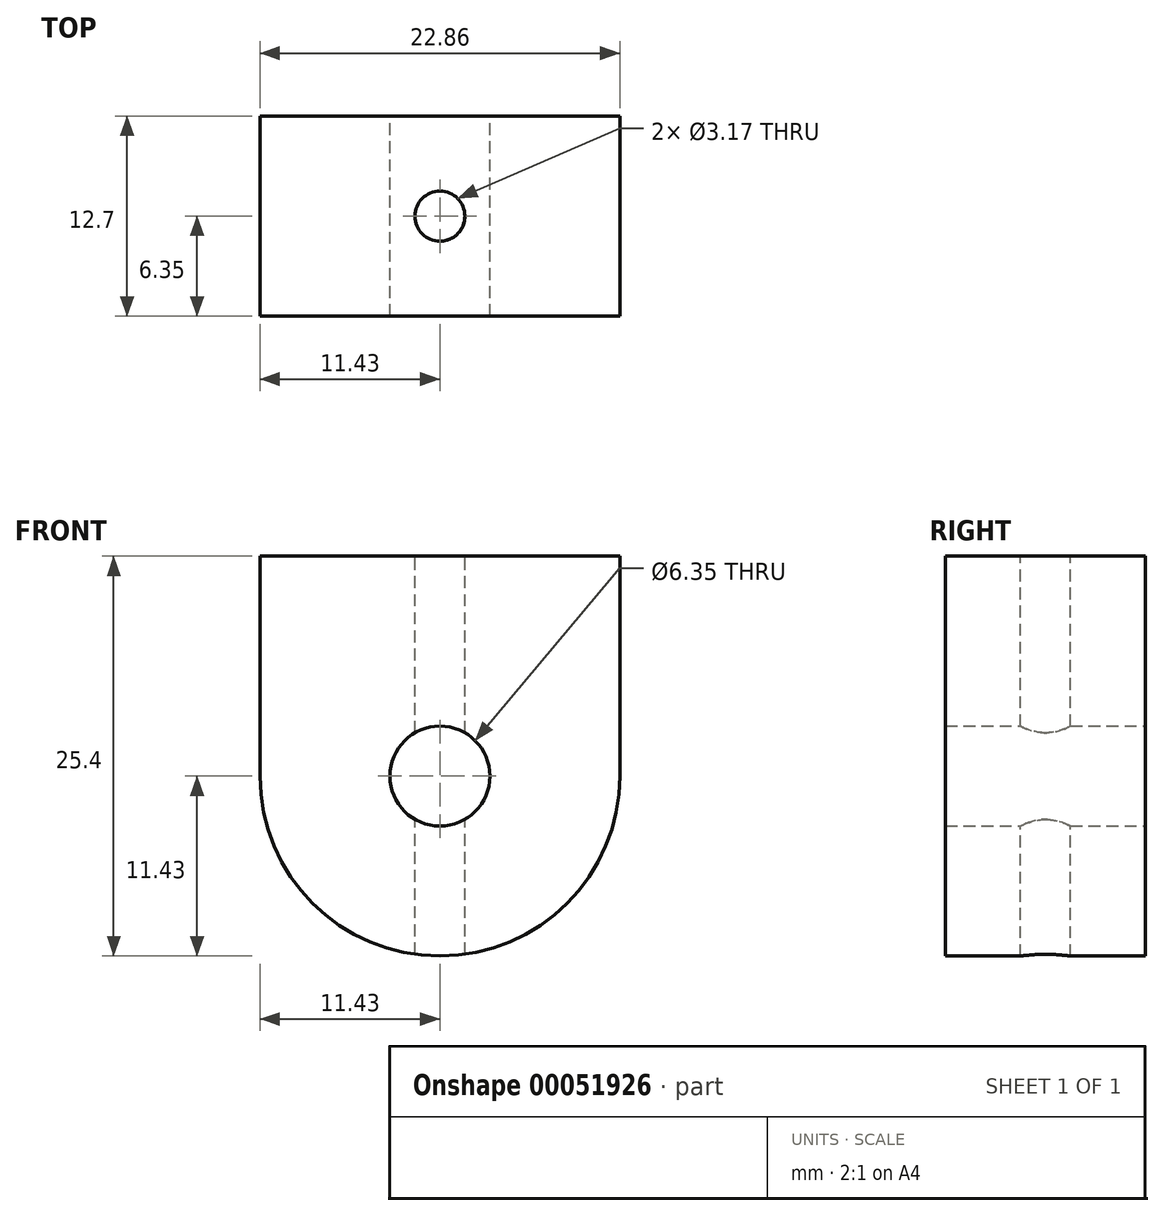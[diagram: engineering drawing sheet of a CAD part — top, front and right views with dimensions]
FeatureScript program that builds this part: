
annotation { "Feature Type Name" : "Feature", "Feature Type Description" : "" }
export const myFeature = defineFeature(function(context is Context, id is Id, definition is map)
    precondition{}
    {
        {
            var Q0;
            Q0=qCreatedBy(makeId("Top.planeOp"),FACE);
            var sketch = newSketch(context, id + "F0", { "sketchPlane" : qUnion([Q0])});
            skLineSegment(sketch, "E0.rect.bottom", {"start": v(12.7, -6.35) * mm, "end": v(-12.7, -6.35) * mm});
            skLineSegment(sketch, "E0.rect.top", {"start": v(12.7, 6.35) * mm, "end": v(-12.7, 6.35) * mm});
            skLineSegment(sketch, "E0.rect.left", {"start": v(12.7, -6.35) * mm, "end": v(12.7, 6.35) * mm});
            skLineSegment(sketch, "E0.rect.right", {"start": v(-12.7, -6.35) * mm, "end": v(-12.7, 6.35) * mm});
            skPoint(sketch, "E0.rect.middle", {"position": v(0, 0) * mm});
            skSolve(sketch);
        }
        {
            var Q0;
            Q0=makeQuery(id+"F0.imprint","IMPRINT",FACE,{"disambiguationData":[TD([[makeQuery(id+"F0.imprint","IMPRINT",EDGE,{"derivedFrom":sQuery(id+"F0.wireOp",EDGE,"E0.rect.bottom")}),-1.0]])]});
            extrude(context, id + "F1", {"entities" : qUnion([Q0]), "depth" : 12.7 * mm});
        }
        {
            var Q0;
            Q0=makeQuery(id+"F1.opExtrude","SWEPT_FACE",FACE,{"disambiguationData":[OSD([sQuery(id+"F0.wireOp",EDGE,"E0.rect.left")])]});
            var sketch = newSketch(context, id + "F2", { "sketchPlane" : qUnion([Q0])});
            skLineSegment(sketch, "E1", {"start": v(-6.35, 12.7) * mm, "end": v(6.35, 0) * mm, "construction": true});
            skLineSegment(sketch, "E2", {"start": v(6.35, 12.7) * mm, "end": v(-6.35, 0) * mm, "construction": true});
            skCircle(sketch, "E3", {"center": v(0, 6.35) * mm, "radius": 1.59 * mm});
            skSolve(sketch);
        }
        {
            var Q0;
            Q0=makeQuery(id+"F2.imprint","IMPRINT",FACE,{"disambiguationData":[TD([[makeQuery(id+"F2.imprint","IMPRINT",EDGE,{"derivedFrom":sQuery(id+"F2.wireOp",EDGE,"E3")}),1.0]])]});
            extrude(context, id + "F3", {"entities" : qUnion([Q0]), "operationType" : NewBodyOperationType.REMOVE, "endBound" : BoundingType.UP_TO_NEXT, "oppositeDirection" : true, "depth" : 25.4 * mm});
        }
        {
            var Q0;
            Q0=qCreatedBy(makeId("Top.planeOp"),FACE);
            var sketch = newSketch(context, id + "F4", { "sketchPlane" : qUnion([Q0])});
            skLineSegment(sketch, "E4.rect.bottom", {"start": v(-38.1, -25.4) * mm, "end": v(38.1, -25.4) * mm});
            skLineSegment(sketch, "E4.rect.top", {"start": v(-38.1, 25.4) * mm, "end": v(38.1, 25.4) * mm});
            skLineSegment(sketch, "E4.rect.left", {"start": v(-38.1, -25.4) * mm, "end": v(-38.1, 25.4) * mm});
            skLineSegment(sketch, "E4.rect.right", {"start": v(38.1, -25.4) * mm, "end": v(38.1, 25.4) * mm});
            skPoint(sketch, "E4.rect.middle", {"position": v(0, 0) * mm});
            skSolve(sketch);
        }
        {
            var Q0;
            Q0=makeQuery(id+"F4.imprint","IMPRINT",FACE,{"disambiguationData":[TD([[makeQuery(id+"F4.imprint","IMPRINT",EDGE,{"derivedFrom":sQuery(id+"F4.wireOp",EDGE,"E4.rect.bottom")}),1.0]])]});
            extrude(context, id + "F5", {"entities" : qUnion([Q0]), "oppositeDirection" : true, "depth" : 1.59 * mm});
        }
        {
            var Q0;
            Q0=qCreatedBy(makeId("Front.planeOp"),FACE);
            var sketch = newSketch(context, id + "F6", { "sketchPlane" : qUnion([Q0])});
            skLineSegment(sketch, "E5.bottom", {"start": v(-12.7, 0) * mm, "end": v(12.7, 0) * mm});
            skLineSegment(sketch, "E5.top", {"start": v(-12.7, 12.7) * mm, "end": v(12.7, 12.7) * mm, "construction": true});
            skLineSegment(sketch, "E5.left", {"start": v(-12.7, 0) * mm, "end": v(-12.7, 12.7) * mm});
            skLineSegment(sketch, "E5.right", {"start": v(12.7, 0) * mm, "end": v(12.7, 12.7) * mm});
            skArc(sketch, "E6", {"start": v(12.7, 12.7) * mm, "mid": v(0, 25.4) * mm, "end": v(-12.7, 12.7) * mm});
            skCircle(sketch, "E7", {"center": v(0, 12.7) * mm, "radius": 3.18 * mm});
            skPoint(sketch, "E8", {"position": v(0, 25.4) * mm});
            skSolve(sketch);
        }
        {
            var Q0;
            Q0=makeQuery(id+"F6.imprint","IMPRINT",FACE,{"disambiguationData":[TD([[makeQuery(id+"F6.imprint","IMPRINT",EDGE,{"derivedFrom":sQuery(id+"F6.wireOp",EDGE,"E5.bottom")}),1.0]])]});
            extrude(context, id + "F7", {"entities" : qUnion([Q0]), "operationType" : NewBodyOperationType.ADD, "depth" : 12.7 * mm, "hasSecondDirection" : true, "secondDirectionOppositeDirection" : true, "secondDirectionDepth" : 12.7 * mm});
        }
        {
            var Q0;
            Q0=qCreatedBy(makeId("Right.planeOp"),FACE);
            var sketch = newSketch(context, id + "F8", { "sketchPlane" : qUnion([Q0])});
            skLineSegment(sketch, "E9.rect.bottom", {"start": v(6.35, 0) * mm, "end": v(-6.35, 0) * mm});
            skLineSegment(sketch, "E9.rect.top", {"start": v(6.35, 65.79) * mm, "end": v(-6.35, 65.79) * mm});
            skLineSegment(sketch, "E9.rect.left", {"start": v(6.35, 0) * mm, "end": v(6.35, 65.79) * mm});
            skLineSegment(sketch, "E9.rect.right", {"start": v(-6.35, 0) * mm, "end": v(-6.35, 65.79) * mm});
            skPoint(sketch, "E9.rect.middle", {"position": v(0, 32.9) * mm});
            skSolve(sketch);
        }
        {
            var Q0;
            Q0=makeQuery(id+"F8.imprint","IMPRINT",FACE,{"disambiguationData":[TD([[makeQuery(id+"F8.imprint","IMPRINT",EDGE,{"derivedFrom":sQuery(id+"F8.wireOp",EDGE,"E9.rect.bottom")}),-1.0]])]});
            extrude(context, id + "F9", {"entities" : qUnion([Q0]), "operationType" : NewBodyOperationType.REMOVE, "endBound" : BoundingType.THROUGH_ALL, "oppositeDirection" : true, "depth" : 25.4 * mm, "hasSecondDirection" : true, "secondDirectionBound" : SecondDirectionBoundingType.THROUGH_ALL, "secondDirectionOppositeDirection" : false, "secondDirectionDepth" : 25.4 * mm});
        }
        {
            var Q0;
            Q0=qCreatedBy(makeId("Front.planeOp"),FACE);
            var sketch = newSketch(context, id + "F10", { "sketchPlane" : qUnion([Q0])});
            skCircle(sketch, "E10.0", {"center": v(0, 12.7) * mm, "radius": 3.18 * mm});
            skLineSegment(sketch, "E11.rect.bottom", {"start": v(11.43, 12.7) * mm, "end": v(-11.43, 12.7) * mm, "construction": true});
            skLineSegment(sketch, "E11.rect.top", {"start": v(11.43, 26.67) * mm, "end": v(-11.43, 26.67) * mm});
            skLineSegment(sketch, "E11.rect.left", {"start": v(11.43, 12.7) * mm, "end": v(11.43, 26.67) * mm});
            skLineSegment(sketch, "E11.rect.right", {"start": v(-11.43, 12.7) * mm, "end": v(-11.43, 26.67) * mm});
            skPoint(sketch, "E11.rect.middle", {"position": v(0, 19.68) * mm});
            skArc(sketch, "E12", {"start": v(-11.43, 12.7) * mm, "mid": v(0, 1.27) * mm, "end": v(11.43, 12.7) * mm});
            skPoint(sketch, "E13", {"position": v(0, 1.27) * mm});
            skSolve(sketch);
        }
        {
            var Q0;
            Q0=makeQuery(id+"F10.imprint","IMPRINT",FACE,{"disambiguationData":[TD([[makeQuery(id+"F10.imprint","IMPRINT",EDGE,{"derivedFrom":sQuery(id+"F10.wireOp",EDGE,"E10.0")}),-1.0]])]});
            extrude(context, id + "F11", {"entities" : qUnion([Q0]), "depth" : 6.35 * mm, "hasSecondDirection" : true, "secondDirectionOppositeDirection" : true, "secondDirectionDepth" : 6.35 * mm});
        }
        {
            var Q0;
            Q0=makeQuery(id+"F11.opExtrude","SWEPT_FACE",FACE,{"disambiguationData":[OSD([sQuery(id+"F10.wireOp",EDGE,"E11.rect.top")])]});
            var sketch = newSketch(context, id + "F12", { "sketchPlane" : qUnion([Q0])});
            skCircle(sketch, "E14", {"center": v(0, 0) * mm, "radius": 1.59 * mm});
            skSolve(sketch);
        }
        {
            var Q0;
            Q0=makeQuery(id+"F12.imprint","IMPRINT",FACE,{"disambiguationData":[TD([[makeQuery(id+"F12.imprint","IMPRINT",EDGE,{"derivedFrom":sQuery(id+"F12.wireOp",EDGE,"E14")}),1.0]])]});
            extrude(context, id + "F13", {"entities" : qUnion([Q0]), "operationType" : NewBodyOperationType.REMOVE, "endBound" : BoundingType.THROUGH_ALL, "oppositeDirection" : true, "depth" : 25.4 * mm});
        }
        {
            var Q0;
            Q0=makeQuery(id+"F1.opExtrude","SWEPT_BODY",BODY,{"disambiguationData":[OSD([sQuery(id+"F0.wireOp",EDGE,"E0.rect.bottom"),sQuery(id+"F0.wireOp",EDGE,"E0.rect.top"),sQuery(id+"F0.wireOp",EDGE,"E0.rect.left"),sQuery(id+"F0.wireOp",EDGE,"E0.rect.right")])]});
            deleteBodies(context, id + "F14", {"entities" : qUnion([Q0])});
        }
    });
